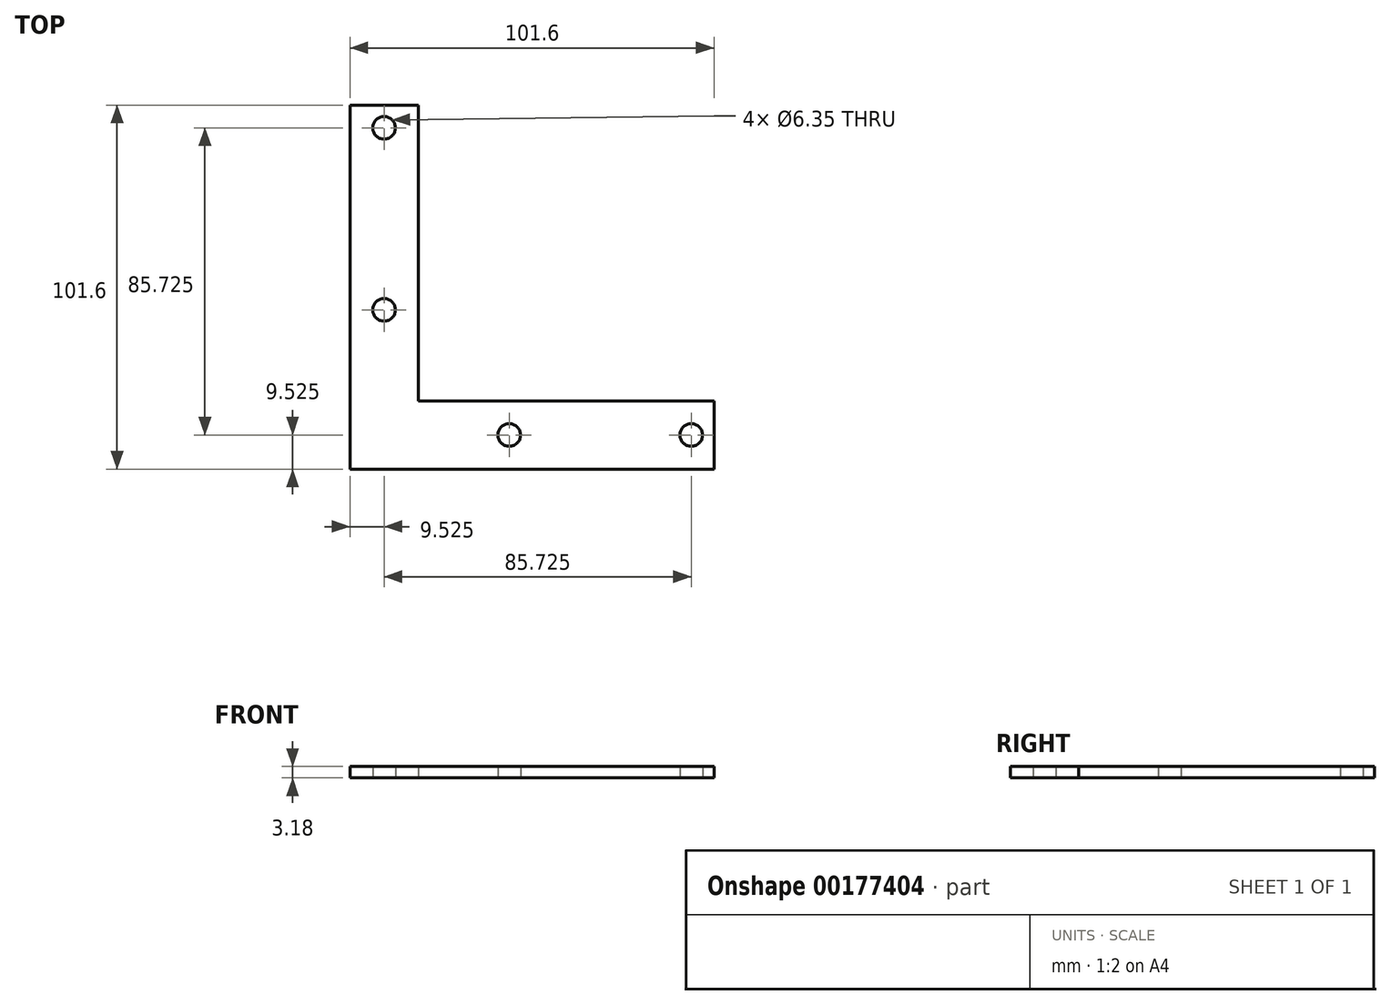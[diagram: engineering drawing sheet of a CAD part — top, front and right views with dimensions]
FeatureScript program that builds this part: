
annotation { "Feature Type Name" : "Feature", "Feature Type Description" : "" }
export const myFeature = defineFeature(function(context is Context, id is Id, definition is map)
    precondition{}
    {
        {
            var Q0;
            Q0=qCreatedBy(makeId("Top.planeOp"),FACE);
            var sketch = newSketch(context, id + "F0", { "sketchPlane" : qUnion([Q0])});
            skLineSegment(sketch, "E0.bottom", {"start": v(-50.8, 50.8) * mm, "end": v(50.8, 50.8) * mm});
            skLineSegment(sketch, "E0.top", {"start": v(-50.8, -50.8) * mm, "end": v(50.8, -50.8) * mm});
            skLineSegment(sketch, "E0.left", {"start": v(-50.8, 50.8) * mm, "end": v(-50.8, -50.8) * mm});
            skLineSegment(sketch, "E0.right", {"start": v(50.8, 50.8) * mm, "end": v(50.8, -50.8) * mm});
            skPoint(sketch, "E0.middle", {"position": v(0, 0) * mm});
            skLineSegment(sketch, "E1", {"start": v(50.8, -31.75) * mm, "end": v(-50.8, -31.75) * mm});
            skLineSegment(sketch, "E2", {"start": v(-31.75, 50.8) * mm, "end": v(-31.75, -50.8) * mm});
            skLineSegment(sketch, "E3", {"start": v(-41.27, 50.8) * mm, "end": v(-41.27, -50.8) * mm});
            skLineSegment(sketch, "E4", {"start": v(-50.8, -41.27) * mm, "end": v(50.8, -41.27) * mm});
            skCircle(sketch, "E5", {"center": v(-41.27, 44.45) * mm, "radius": 3.18 * mm});
            skCircle(sketch, "E6", {"center": v(-41.27, -6.35) * mm, "radius": 3.18 * mm});
            skCircle(sketch, "E7", {"center": v(44.45, -41.27) * mm, "radius": 3.18 * mm});
            skCircle(sketch, "E8", {"center": v(-6.35, -41.27) * mm, "radius": 3.18 * mm});
            skSolve(sketch);
        }
        {
            var Q0;
            {var subQ0=sQuery(id+"F0.wireOp",EDGE,"E2");var subQ1=sQuery(id+"F0.wireOp",EDGE,"E0.bottom");var subQ2=makeQuery(id+"F0.imprint","INTERSECT",VERTEX,{"derivedFrom":[subQ1,subQ0]});Q0=makeQuery(id+"F0.imprint","IMPRINT",FACE,{"disambiguationData":[TD([[makeQuery(id+"F0.imprint","IMPRINT",EDGE,{"disambiguationData":[TD([[subQ2,1.0]])],"derivedFrom":subQ1}),-1.0]])]});}
            var Q1;
            {var subQ1=sQuery(id+"F0.wireOp",EDGE,"E0.left");var subQ5=sQuery(id+"F0.wireOp",EDGE,"E0.bottom");var subQ9=makeQuery(id+"F0.imprint","INTERSECT",VERTEX,{"derivedFrom":[subQ5,subQ1]});Q1=makeQuery(id+"F0.imprint","IMPRINT",FACE,{"disambiguationData":[TD([[makeQuery(id+"F0.imprint","IMPRINT",EDGE,{"disambiguationData":[TD([[subQ9,-1.0]])],"derivedFrom":subQ5}),-1.0]])]});}
            var Q2;
            {var subQ0=sQuery(id+"F0.wireOp",EDGE,"E2");var subQ1=sQuery(id+"F0.wireOp",EDGE,"E1");var subQ2=makeQuery(id+"F0.imprint","INTERSECT",VERTEX,{"derivedFrom":[subQ1,subQ0]});Q2=makeQuery(id+"F0.imprint","IMPRINT",FACE,{"disambiguationData":[TD([[makeQuery(id+"F0.imprint","IMPRINT",EDGE,{"disambiguationData":[TD([[subQ2,-1.0]])],"derivedFrom":subQ1}),1.0]])]});}
            var Q3;
            {var subQ0=sQuery(id+"F0.wireOp",EDGE,"E1");var subQ1=sQuery(id+"F0.wireOp",EDGE,"E0.left");var subQ2=makeQuery(id+"F0.imprint","INTERSECT",VERTEX,{"derivedFrom":[subQ1,subQ0]});Q3=makeQuery(id+"F0.imprint","IMPRINT",FACE,{"disambiguationData":[TD([[makeQuery(id+"F0.imprint","IMPRINT",EDGE,{"disambiguationData":[TD([[subQ2,-1.0]])],"derivedFrom":subQ1}),1.0]])]});}
            var Q4;
            {var subQ0=sQuery(id+"F0.wireOp",EDGE,"E0.left");var subQ1=sQuery(id+"F0.wireOp",EDGE,"E0.top");var subQ2=makeQuery(id+"F0.imprint","INTERSECT",VERTEX,{"derivedFrom":[subQ1,subQ0]});Q4=makeQuery(id+"F0.imprint","IMPRINT",FACE,{"disambiguationData":[TD([[makeQuery(id+"F0.imprint","IMPRINT",EDGE,{"disambiguationData":[TD([[subQ2,-1.0]])],"derivedFrom":subQ1}),1.0]])]});}
            var Q5;
            {var subQ0=sQuery(id+"F0.wireOp",EDGE,"E2");var subQ1=sQuery(id+"F0.wireOp",EDGE,"E0.top");var subQ2=makeQuery(id+"F0.imprint","INTERSECT",VERTEX,{"derivedFrom":[subQ1,subQ0]});Q5=makeQuery(id+"F0.imprint","IMPRINT",FACE,{"disambiguationData":[TD([[makeQuery(id+"F0.imprint","IMPRINT",EDGE,{"disambiguationData":[TD([[subQ2,1.0]])],"derivedFrom":subQ1}),1.0]])]});}
            var Q6;
            {var subQ5=sQuery(id+"F0.wireOp",EDGE,"E0.top");var subQ7=sQuery(id+"F0.wireOp",EDGE,"E0.right");var subQ12=makeQuery(id+"F0.imprint","INTERSECT",VERTEX,{"derivedFrom":[subQ5,subQ7]});Q6=makeQuery(id+"F0.imprint","IMPRINT",FACE,{"disambiguationData":[TD([[makeQuery(id+"F0.imprint","IMPRINT",EDGE,{"disambiguationData":[TD([[subQ12,1.0]])],"derivedFrom":subQ5}),1.0]])]});}
            var Q7;
            {var subQ1=sQuery(id+"F0.wireOp",EDGE,"E1");var subQ5=sQuery(id+"F0.wireOp",EDGE,"E0.right");var subQ6=makeQuery(id+"F0.imprint","INTERSECT",VERTEX,{"derivedFrom":[subQ5,subQ1]});Q7=makeQuery(id+"F0.imprint","IMPRINT",FACE,{"disambiguationData":[TD([[makeQuery(id+"F0.imprint","IMPRINT",EDGE,{"disambiguationData":[TD([[subQ6,-1.0]])],"derivedFrom":subQ5}),-1.0]])]});}
            extrude(context, id + "F1", {"entities" : qUnion([Q0, Q1, Q2, Q3, Q4, Q5, Q6, Q7]), "depth" : 3.17 * mm});
        }
    });
